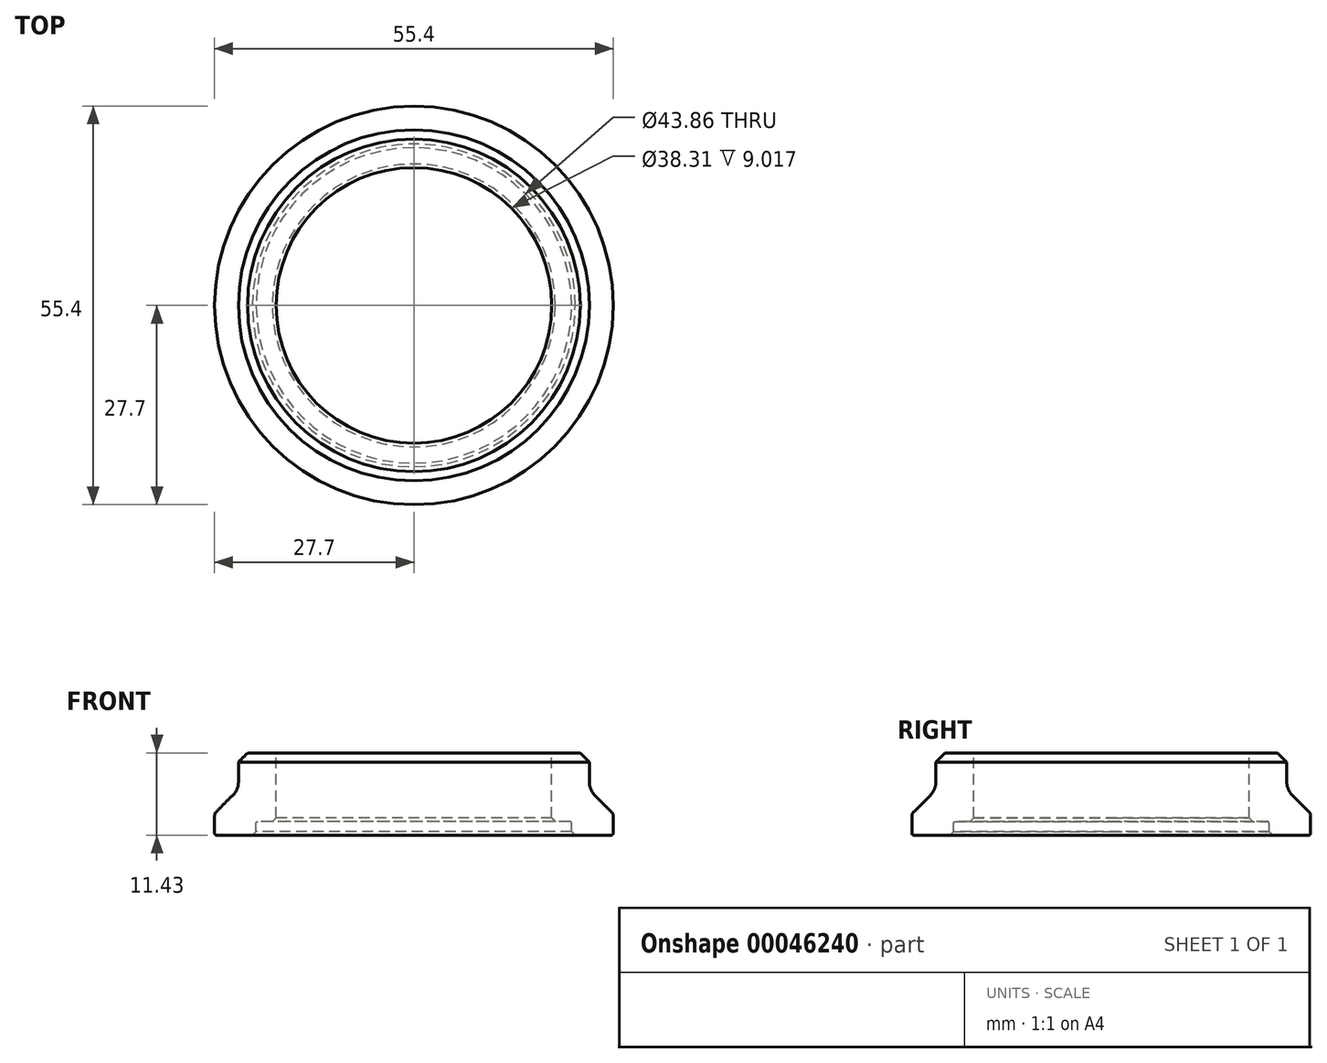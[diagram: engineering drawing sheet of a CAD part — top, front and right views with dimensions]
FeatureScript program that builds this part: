
annotation { "Feature Type Name" : "Feature", "Feature Type Description" : "" }
export const myFeature = defineFeature(function(context is Context, id is Id, definition is map)
    precondition{}
    {
        {
            var Q0;
            Q0=qCreatedBy(makeId("Front.planeOp"),FACE);
            var sketch = newSketch(context, id + "F0", { "sketchPlane" : qUnion([Q0])});
            skLineSegment(sketch, "E0", {"start": v(-27.7, -3.81) * mm, "end": v(-27.7, -0.78) * mm});
            skLineSegment(sketch, "E1", {"start": v(-27.7, -0.78) * mm, "end": v(-24.38, 2.53) * mm});
            skLineSegment(sketch, "E2", {"start": v(-24.38, 2.53) * mm, "end": v(-24.38, 7.62) * mm});
            skLineSegment(sketch, "E3", {"start": v(-24.38, 7.62) * mm, "end": v(-19.15, 7.62) * mm});
            skLineSegment(sketch, "E4", {"start": v(-19.15, 7.62) * mm, "end": v(-19.15, -1.9) * mm});
            skLineSegment(sketch, "E5", {"start": v(-19.15, -1.9) * mm, "end": v(-21.93, -1.9) * mm});
            skLineSegment(sketch, "E6", {"start": v(-21.93, -1.9) * mm, "end": v(-21.93, -3.81) * mm});
            skLineSegment(sketch, "E7", {"start": v(-21.93, -3.81) * mm, "end": v(-27.7, -3.81) * mm});
            skLineSegment(sketch, "E8", {"start": v(0, 32.35) * mm, "end": v(0, -20.35) * mm, "construction": true});
            skSolve(sketch);
        }
        {
            var Q0;
            Q0=makeQuery(id+"F0.imprint","IMPRINT",FACE,{"disambiguationData":[TD([[makeQuery(id+"F0.imprint","IMPRINT",EDGE,{"derivedFrom":sQuery(id+"F0.wireOp",EDGE,"E0")}),-1.0]])]});
            var Q1;
            Q1=sQuery(id+"F0.wireOp",EDGE,"E8");
            revolve(context, id + "F6", {"entities" : qUnion([Q0]), "axis" : qUnion([Q1]), "revolveType" : RevolveType.FULL});
        }
        {
            var Q0;
            Q0=makeQuery(id+"F6.opRevolve","SWEPT_EDGE",EDGE,{"disambiguationData":[OSD([sQuery(id+"F0.wireOp",EDGE,"E0"),sQuery(id+"F0.wireOp",EDGE,"E1")])]});
            fillet(context, id + "F1", {"entities" : qUnion([Q0]), "radius" : 0.76 * mm, "tangentPropagation" : true, "allowEdgeOverflow" : false});
        }
        {
            var Q0;
            Q0=makeQuery(id+"F6.opRevolve","SWEPT_EDGE",EDGE,{"disambiguationData":[OSD([sQuery(id+"F0.wireOp",EDGE,"E1"),sQuery(id+"F0.wireOp",EDGE,"E2")])]});
            fillet(context, id + "F2", {"entities" : qUnion([Q0]), "radius" : 2.54 * mm, "tangentPropagation" : true, "allowEdgeOverflow" : false});
        }
        {
            var Q0;
            Q0=makeQuery(id+"F6.opRevolve","SWEPT_EDGE",EDGE,{"disambiguationData":[OSD([sQuery(id+"F0.wireOp",EDGE,"E0"),sQuery(id+"F0.wireOp",EDGE,"E7")])]});
            fillet(context, id + "F7", {"entities" : qUnion([Q0]), "radius" : 0.25 * mm, "tangentPropagation" : true, "allowEdgeOverflow" : false});
        }
        {
            var Q0;
            Q0=makeQuery(id+"F6.opRevolve","SWEPT_EDGE",EDGE,{"disambiguationData":[OSD([sQuery(id+"F0.wireOp",EDGE,"E6"),sQuery(id+"F0.wireOp",EDGE,"E7")])]});
            var Q1;
            Q1=makeQuery(id+"F6.opRevolve","SWEPT_EDGE",EDGE,{"disambiguationData":[OSD([sQuery(id+"F0.wireOp",EDGE,"E4"),sQuery(id+"F0.wireOp",EDGE,"E5")])]});
            chamfer(context, id + "F3", {"entities" : qUnion([Q0, Q1]), "width" : 0.5 * mm, "tangentPropagation" : true});
        }
        {
            var Q0;
            Q0=makeQuery(id+"F6.opRevolve","SWEPT_EDGE",EDGE,{"disambiguationData":[OSD([sQuery(id+"F0.wireOp",EDGE,"E5"),sQuery(id+"F0.wireOp",EDGE,"E6")])]});
            fillet(context, id + "F4", {"entities" : qUnion([Q0]), "radius" : 0.25 * mm, "tangentPropagation" : true, "allowEdgeOverflow" : false});
        }
        {
            var Q0;
            Q0=makeQuery(id+"F6.opRevolve","SWEPT_EDGE",EDGE,{"disambiguationData":[OSD([sQuery(id+"F0.wireOp",EDGE,"E2"),sQuery(id+"F0.wireOp",EDGE,"E3")])]});
            chamfer(context, id + "F5", {"entities" : qUnion([Q0]), "width" : 1.27 * mm, "tangentPropagation" : true});
        }
    });
